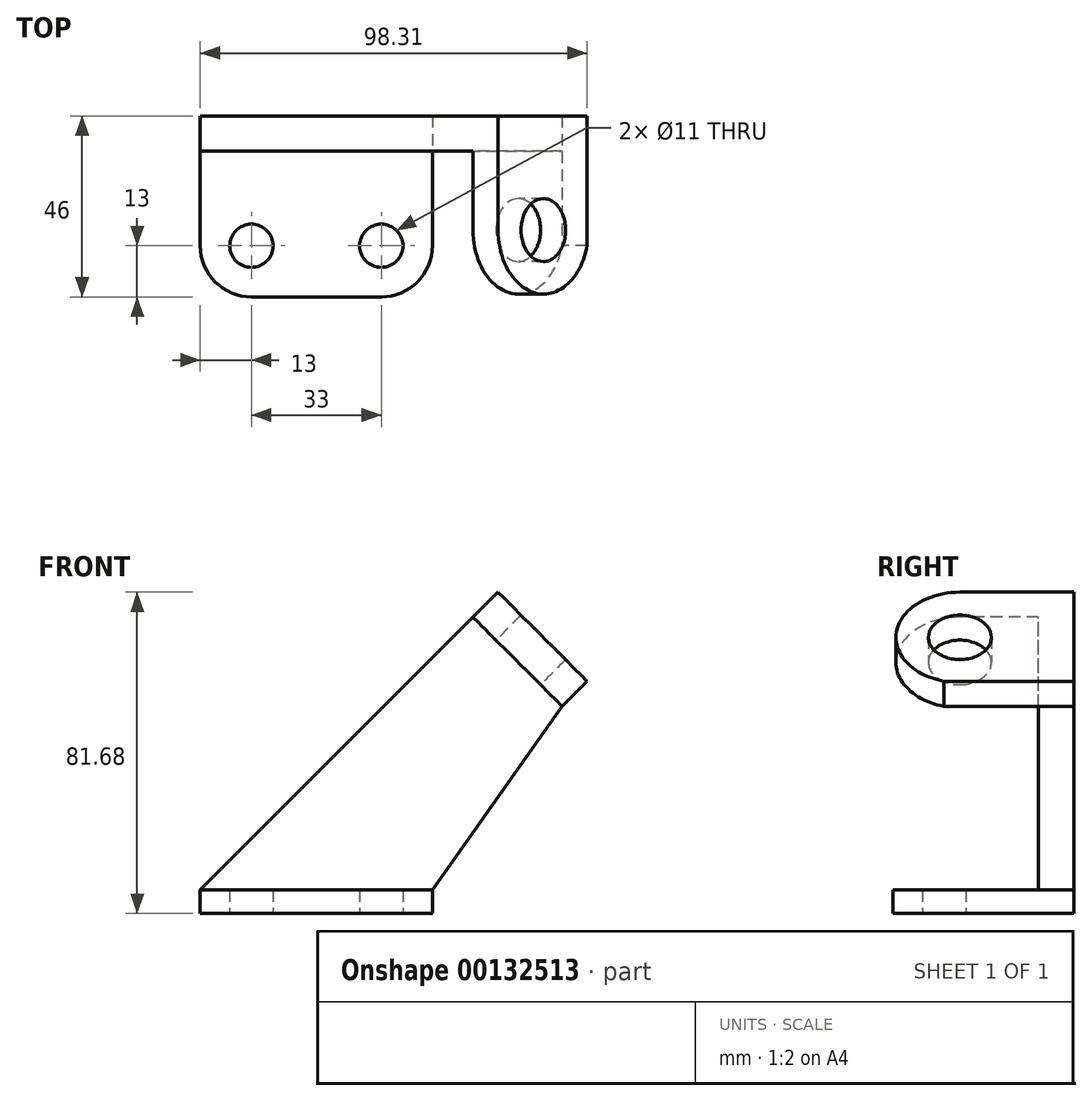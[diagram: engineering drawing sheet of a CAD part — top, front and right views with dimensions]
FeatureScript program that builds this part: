
annotation { "Feature Type Name" : "Feature", "Feature Type Description" : "" }
export const myFeature = defineFeature(function(context is Context, id is Id, definition is map)
    precondition{}
    {
        {
            var Q0;
            Q0=qCreatedBy(makeId("Top.planeOp"),FACE);
            var sketch = newSketch(context, id + "F0", { "sketchPlane" : qUnion([Q0])});
            skLineSegment(sketch, "E0", {"start": v(0, 24) * mm, "end": v(0, 0) * mm});
            skLineSegment(sketch, "E1", {"start": v(0, 24) * mm, "end": v(59, 24) * mm});
            skLineSegment(sketch, "E2", {"start": v(59, 24) * mm, "end": v(59, 0) * mm});
            skLineSegment(sketch, "E3", {"start": v(13, -13) * mm, "end": v(46, -13) * mm});
            skArc(sketch, "E4", {"start": v(0, 0) * mm, "mid": v(3.8, -9.2) * mm, "end": v(13, -13) * mm});
            skArc(sketch, "E5", {"start": v(46, -13) * mm, "mid": v(55.2, -9.2) * mm, "end": v(59, 0) * mm});
            skCircle(sketch, "E6", {"center": v(13, 0) * mm, "radius": 5.5 * mm});
            skCircle(sketch, "E7", {"center": v(46, 0) * mm, "radius": 5.5 * mm});
            skSolve(sketch);
        }
        {
            var Q0;
            Q0 = qSketchRegion(id + "F0", true);
            extrude(context, id + "F1", {"entities" : qUnion([Q0]), "depth" : 6 * mm});
        }
        {
            var Q0;
            Q0=makeQuery(id+"F1.opExtrude","SWEPT_FACE",FACE,{"disambiguationData":[OSD([sQuery(id+"F0.wireOp",EDGE,"E1")])]});
            var sketch = newSketch(context, id + "F2", { "sketchPlane" : qUnion([Q0])});
            skLineSegment(sketch, "E8", {"start": v(-59, 6) * mm, "end": v(-91.94, 52.69) * mm});
            skLineSegment(sketch, "E9", {"start": v(0, 6) * mm, "end": v(-69.31, 75.31) * mm});
            skLineSegment(sketch, "E10", {"start": v(-91.94, 52.69) * mm, "end": v(-69.31, 75.31) * mm});
            skLineSegment(sketch, "E11", {"start": v(-59, 6) * mm, "end": v(-59, 0) * mm});
            skLineSegment(sketch, "E12", {"start": v(-59, 0) * mm, "end": v(0, 0) * mm});
            skLineSegment(sketch, "E13", {"start": v(0, 0) * mm, "end": v(0, 6) * mm});
            skLineSegment(sketch, "E14", {"start": v(-69.31, 75.31) * mm, "end": v(-92.52, 75.31) * mm, "construction": true});
            skPoint(sketch, "E15", {"position": v(-80.63, 64) * mm});
            skSolve(sketch);
        }
        {
            var Q0;
            Q0 = qSketchRegion(id + "F2", true);
            extrude(context, id + "F3", {"entities" : qUnion([Q0]), "operationType" : NewBodyOperationType.ADD, "depth" : 9 * mm});
        }
        {
            var Q0;
            Q0=makeQuery(id+"F3.opExtrude","SWEPT_FACE",FACE,{"disambiguationData":[OSD([sQuery(id+"F2.wireOp",EDGE,"E10")])]});
            var sketch = newSketch(context, id + "F4", { "sketchPlane" : qUnion([Q0])});
            skArc(sketch, "E16", {"start": v(4, 4.24) * mm, "mid": v(-12.12, -10) * mm, "end": v(0, -27.76) * mm});
            skCircle(sketch, "E17", {"center": v(4, -12) * mm, "radius": 8 * mm});
            skLineSegment(sketch, "E18", {"start": v(33, 4.24) * mm, "end": v(33, -27.76) * mm});
            skLineSegment(sketch, "E19", {"start": v(33, 4.24) * mm, "end": v(4, 4.24) * mm});
            skLineSegment(sketch, "E20", {"start": v(33, -27.76) * mm, "end": v(0, -27.76) * mm});
            skSolve(sketch);
        }
        {
            var Q0;
            Q0 = qSketchRegion(id + "F4", true);
            extrude(context, id + "F5", {"entities" : qUnion([Q0]), "operationType" : NewBodyOperationType.ADD, "depth" : 9 * mm});
        }
    });
